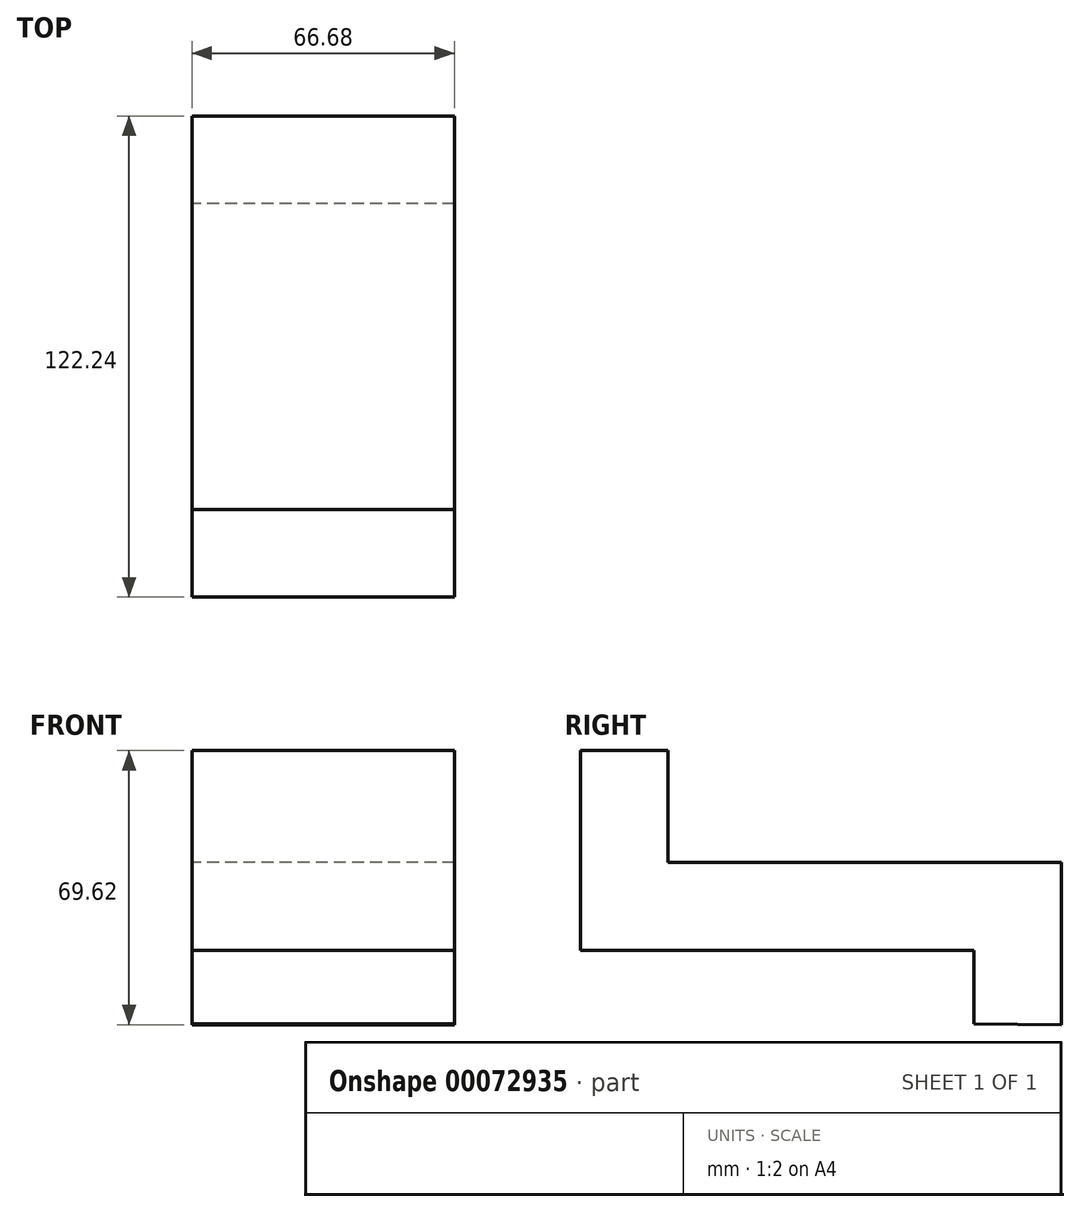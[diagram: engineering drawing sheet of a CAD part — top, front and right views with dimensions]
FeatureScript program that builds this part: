
annotation { "Feature Type Name" : "Feature", "Feature Type Description" : "" }
export const myFeature = defineFeature(function(context is Context, id is Id, definition is map)
    precondition{}
    {
        {
            var Q0;
            Q0=qCreatedBy(makeId("Right.planeOp"),FACE);
            var sketch = newSketch(context, id + "F0", { "sketchPlane" : qUnion([Q0])});
            skLineSegment(sketch, "E0", {"start": v(46.94, -34.19) * mm, "end": v(46.94, 7.09) * mm});
            skLineSegment(sketch, "E1", {"start": v(46.94, 7.09) * mm, "end": v(-53.08, 7.09) * mm});
            skLineSegment(sketch, "E2", {"start": v(-53.08, 7.09) * mm, "end": v(-53.08, 35.43) * mm});
            skLineSegment(sketch, "E3", {"start": v(-53.08, 35.43) * mm, "end": v(-75.3, 35.43) * mm});
            skLineSegment(sketch, "E4", {"start": v(-75.3, 35.43) * mm, "end": v(-75.3, -15.37) * mm});
            skLineSegment(sketch, "E5", {"start": v(-75.3, -15.37) * mm, "end": v(24.71, -15.37) * mm});
            skLineSegment(sketch, "E6", {"start": v(24.71, -15.37) * mm, "end": v(24.71, -34.03) * mm});
            skLineSegment(sketch, "E7", {"start": v(24.71, -34.03) * mm, "end": v(46.94, -34.19) * mm});
            skSolve(sketch);
        }
        {
            var Q0;
            Q0=makeQuery(id+"F0.imprint","IMPRINT",FACE,{"disambiguationData":[TD([[makeQuery(id+"F0.imprint","IMPRINT",EDGE,{"derivedFrom":sQuery(id+"F0.wireOp",EDGE,"E0")}),1.0]])]});
            extrude(context, id + "F1", {"entities" : qUnion([Q0]), "depth" : 33.34 * mm, "hasSecondDirection" : true, "secondDirectionOppositeDirection" : true, "secondDirectionDepth" : 33.34 * mm});
        }
    });
